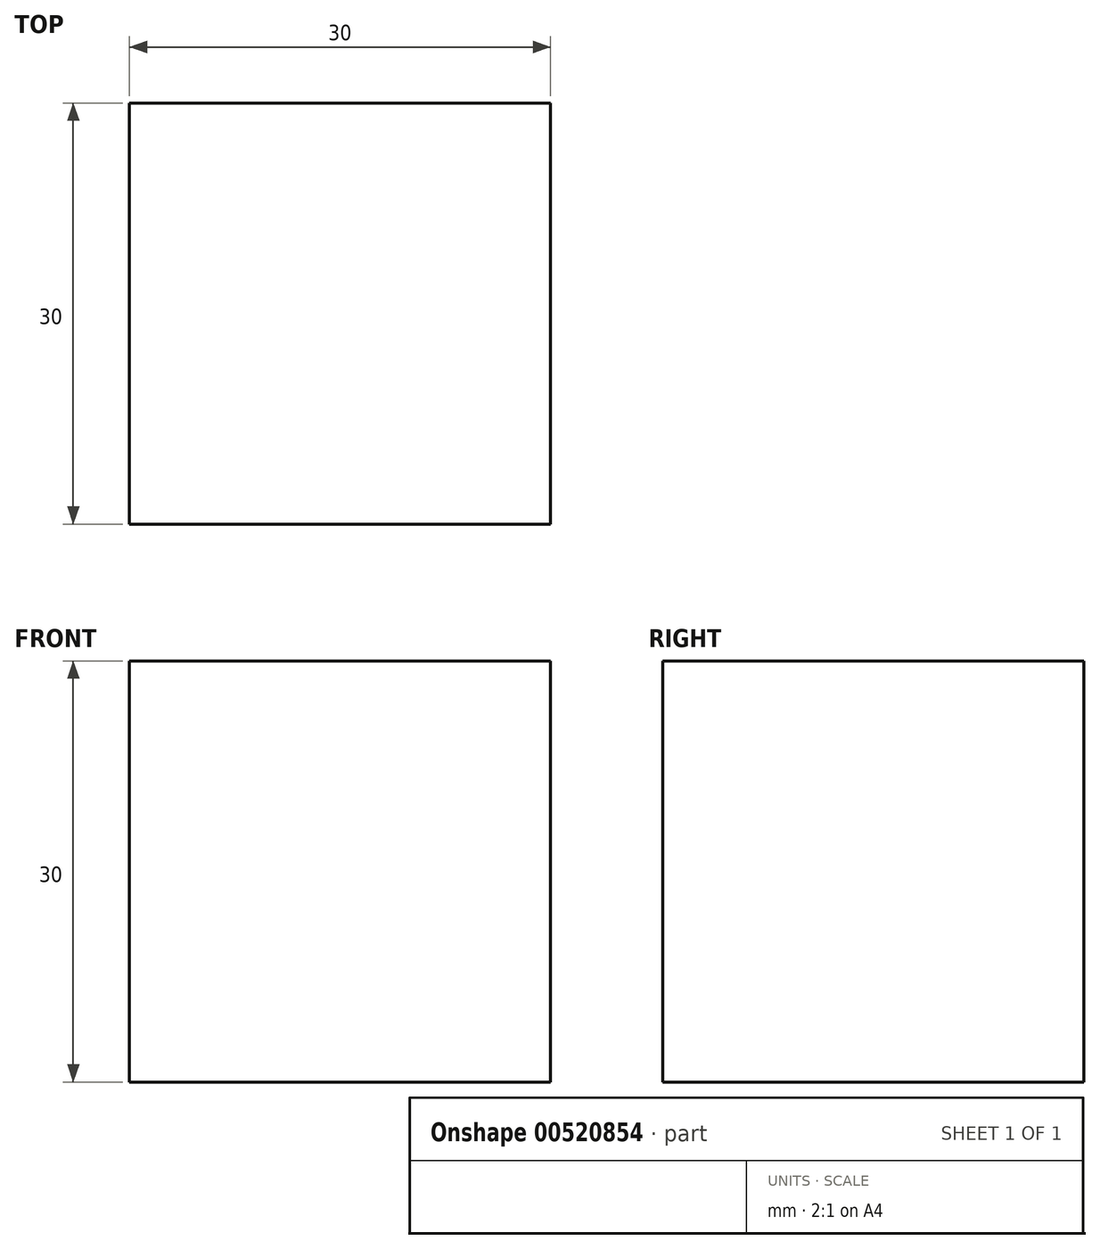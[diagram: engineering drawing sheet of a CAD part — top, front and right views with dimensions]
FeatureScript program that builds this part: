
annotation { "Feature Type Name" : "Feature", "Feature Type Description" : "" }
export const myFeature = defineFeature(function(context is Context, id is Id, definition is map)
    precondition{}
    {
        {
            var Q0;
            Q0=qCreatedBy(makeId("Top.planeOp"),FACE);
            var sketch = newSketch(context, id + "F0", { "sketchPlane" : qUnion([Q0])});
            skLineSegment(sketch, "E0.bottom", {"start": v(-55.36, -46.5) * mm, "end": v(-25.36, -46.5) * mm});
            skLineSegment(sketch, "E0.top", {"start": v(-55.36, -16.5) * mm, "end": v(-25.36, -16.5) * mm});
            skLineSegment(sketch, "E0.left", {"start": v(-55.36, -46.5) * mm, "end": v(-55.36, -16.5) * mm});
            skLineSegment(sketch, "E0.right", {"start": v(-25.36, -46.5) * mm, "end": v(-25.36, -16.5) * mm});
            skSolve(sketch);
        }
        {
            var Q0;
            Q0=makeQuery(id+"F0.imprint","IMPRINT",FACE,{"disambiguationData":[TD([[makeQuery(id+"F0.imprint","IMPRINT",EDGE,{"derivedFrom":sQuery(id+"F0.wireOp",EDGE,"E0.bottom")}),1.0]])]});
            extrude(context, id + "F1", {"entities" : qUnion([Q0]), "depth" : 30 * mm, "offsetDistance" : 25 * mm});
        }
    });
